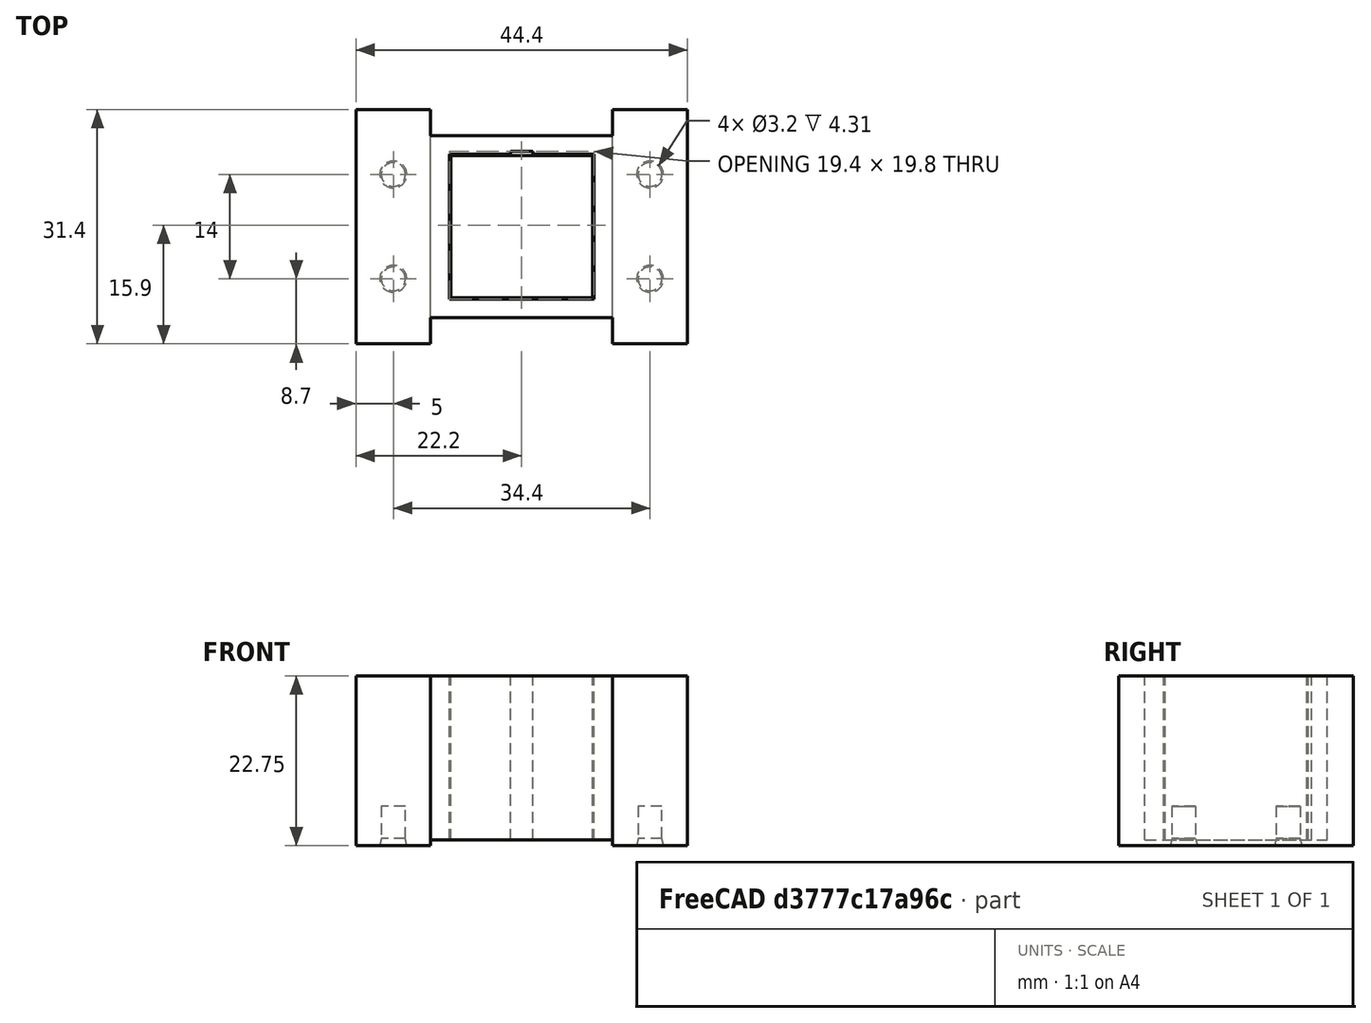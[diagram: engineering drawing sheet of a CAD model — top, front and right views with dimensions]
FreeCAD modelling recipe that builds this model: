
FCSTD DOCUMENT  (FreeCAD 1.0R39319 (Git))
Label: Main
License: All rights reserved
LicenseURL: https://en.wikipedia.org/wiki/All_rights_reserved
objects: Part::Fuse×20, Part::Box×12, Part::Cylinder×8, Part::Cone×4, Mesh::Feature×4, Part::Feature×4, Part::Cut×3, Part::MultiFuse×1
note: 52 computed .brp shape members not serialized (recipe doc carries the construction recipe); baked Part::Feature solids carry a one-line shape summary decoded from their .brp

FEATURE [Part::Box] cube
  AttacherType = Attacher::AttachEngine3D
  Height = 22
  Length = 24.4
  Placement = pos=(-12.2,-12.2,-11) rot=(0,0,1;0rad)
  Width = 24.4
FEATURE [Part::Box] cube001
  AttacherType = Attacher::AttachEngine3D
  Height = 23
  Length = 19.4
  Placement = pos=(-9.7,-9.7,-11.5) rot=(0,0,1;0rad)
  Width = 19.4
FEATURE [Part::Box] cube002
  AttacherType = Attacher::AttachEngine3D
  Height = 23
  Length = 3
  Placement = pos=(-1.5,9.7,-11.5) rot=(0,0,1;0rad)
  Width = 0.4
FEATURE [Part::Fuse] union
  Base = -> cube001
  Refine = true
  Tool = -> cube002
FEATURE [Part::Cut] difference
  Base = -> cube
  Placement = pos=(0,0,11.75) rot=(0,0,1;0rad)
  Refine = true
  Tool = -> union
FEATURE [Part::Box] cube003
  AttacherType = Attacher::AttachEngine3D
  Height = 22.75
  Length = 10
  Placement = pos=(-22.2,-15.7,0) rot=(0,0,1;0rad)
  Width = 31.4
FEATURE [Part::Cylinder] cylinder
  Angle = 360
  AttacherType = Attacher::AttachEngine3D
  FirstAngle = 0
  Height = 6
  Placement = pos=(-17.2,-7,0) rot=(0,0,1;0rad)
  Radius = 3.6
  SecondAngle = 0
FEATURE [Part::Cylinder] cylinder001
  Angle = 360
  AttacherType = Attacher::AttachEngine3D
  FirstAngle = 0
  Height = 6
  Placement = pos=(-17.2,7,0) rot=(0,0,1;0rad)
  Radius = 3.6
  SecondAngle = 0
FEATURE [Part::Fuse] Group
  Base = -> cylinder
  Refine = true
  Tool = -> cylinder001
FEATURE [Part::Fuse] union001
  Base = -> cube003
  Refine = true
  Tool = -> Group
FEATURE [Part::Cylinder] cylinder002
  Angle = 360
  AttacherType = Attacher::AttachEngine3D
  FirstAngle = 0
  Height = 5.32
  Placement = pos=(0,0,-0.01) rot=(0,0,1;0rad)
  Radius = 1.6
  SecondAngle = 0
FEATURE [Part::Cone] cylinder003
  Angle = 360
  AttacherType = Attacher::AttachEngine3D
  Height = 1
  Radius1 = 1.8
  Radius2 = 1.6
FEATURE [Part::Fuse] union002
  Base = -> cylinder002
  Placement = pos=(-17.2,-7,0) rot=(0,0,1;0rad)
  Refine = true
  Tool = -> cylinder003
FEATURE [Part::Cylinder] cylinder004
  Angle = 360
  AttacherType = Attacher::AttachEngine3D
  FirstAngle = 0
  Height = 5.32
  Placement = pos=(0,0,-0.01) rot=(0,0,1;0rad)
  Radius = 1.6
  SecondAngle = 0
FEATURE [Part::Cone] cylinder005
  Angle = 360
  AttacherType = Attacher::AttachEngine3D
  Height = 1
  Radius1 = 1.8
  Radius2 = 1.6
FEATURE [Part::Fuse] union003
  Base = -> cylinder004
  Placement = pos=(-17.2,7,0) rot=(0,0,1;0rad)
  Refine = true
  Tool = -> cylinder005
FEATURE [Part::Fuse] Group001
  Base = -> union002
  Refine = true
  Tool = -> union003
FEATURE [Part::Cut] difference001
  Base = -> union001
  Refine = true
  Tool = -> Group001
FEATURE [Part::Box] cube004
  AttacherType = Attacher::AttachEngine3D
  Height = 22.75
  Length = 10
  Placement = pos=(12.2,-15.7,0) rot=(0,0,1;0rad)
  Width = 31.4
FEATURE [Part::Cylinder] cylinder006
  Angle = 360
  AttacherType = Attacher::AttachEngine3D
  FirstAngle = 0
  Height = 6
  Placement = pos=(17.2,-7,0) rot=(0,0,1;0rad)
  Radius = 3.6
  SecondAngle = 0
FEATURE [Part::Cylinder] cylinder007
  Angle = 360
  AttacherType = Attacher::AttachEngine3D
  FirstAngle = 0
  Height = 6
  Placement = pos=(17.2,7,0) rot=(0,0,1;0rad)
  Radius = 3.6
  SecondAngle = 0
FEATURE [Part::Fuse] Group002
  Base = -> cylinder006
  Refine = true
  Tool = -> cylinder007
FEATURE [Part::Fuse] union004
  Base = -> cube004
  Refine = true
  Tool = -> Group002
FEATURE [Part::Cylinder] cylinder008
  Angle = 360
  AttacherType = Attacher::AttachEngine3D
  FirstAngle = 0
  Height = 5.32
  Placement = pos=(0,0,-0.01) rot=(0,0,1;0rad)
  Radius = 1.6
  SecondAngle = 0
FEATURE [Part::Cone] cylinder009
  Angle = 360
  AttacherType = Attacher::AttachEngine3D
  Height = 1
  Radius1 = 1.8
  Radius2 = 1.6
FEATURE [Part::Fuse] union005
  Base = -> cylinder008
  Placement = pos=(17.2,-7,0) rot=(0,0,1;0rad)
  Refine = true
  Tool = -> cylinder009
FEATURE [Part::Cylinder] cylinder010
  Angle = 360
  AttacherType = Attacher::AttachEngine3D
  FirstAngle = 0
  Height = 5.32
  Placement = pos=(0,0,-0.01) rot=(0,0,1;0rad)
  Radius = 1.6
  SecondAngle = 0
FEATURE [Part::Cone] cylinder011
  Angle = 360
  AttacherType = Attacher::AttachEngine3D
  Height = 1
  Radius1 = 1.8
  Radius2 = 1.6
FEATURE [Part::Fuse] union006
  Base = -> cylinder010
  Placement = pos=(17.2,7,0) rot=(0,0,1;0rad)
  Refine = true
  Tool = -> cylinder011
FEATURE [Part::Fuse] Group003
  Base = -> union005
  Refine = true
  Tool = -> union006
FEATURE [Part::Cut] difference002
  Base = -> union004
  Refine = true
  Tool = -> Group003
FEATURE [Part::Fuse] Group004
  Base = -> difference001
  Refine = true
  Tool = -> difference002
FEATURE [Part::Fuse] union007
  Base = -> difference
  Refine = true
  Tool = -> Group004
FEATURE [Part::Box] cube005
  AttacherType = Attacher::AttachEngine3D
  Height = 22
  Length = 19
  Placement = pos=(-9.5,-9.5,-11) rot=(0,0,1;0rad)
  Width = 19
FEATURE [Part::Box] cube006
  AttacherType = Attacher::AttachEngine3D
  Height = 22
  Length = 8
  Placement = pos=(-8.5,-8.5,-11) rot=(0,0,1;0rad)
  Width = 8
FEATURE [Part::Box] cube007
  AttacherType = Attacher::AttachEngine3D
  Height = 22
  Length = 8
  Placement = pos=(-8.5,0.5,-11) rot=(0,0,1;0rad)
  Width = 8
FEATURE [Part::Fuse] Group005
  Base = -> cube006
  Refine = true
  Tool = -> cube007
FEATURE [Part::Box] cube008
  AttacherType = Attacher::AttachEngine3D
  Height = 22
  Length = 8
  Placement = pos=(0.5,-8.5,-11) rot=(0,0,1;0rad)
  Width = 8
FEATURE [Part::Box] cube009
  AttacherType = Attacher::AttachEngine3D
  Height = 22
  Length = 8
  Placement = pos=(0.5,0.5,-11) rot=(0,0,1;0rad)
  Width = 8
FEATURE [Part::Fuse] Group006
  Base = -> cube008
  Refine = true
  Tool = -> cube009
FEATURE [Part::Fuse] Group007
  Base = -> Group005
  Refine = true
  Tool = -> Group006
FEATURE [Part::Box] cube010
  AttacherType = Attacher::AttachEngine3D
  Height = 22
  Length = 1
  Placement = pos=(-0.5,-9,-11) rot=(0,0,1;0rad)
  Width = 18
FEATURE [Part::Box] cube011
  AttacherType = Attacher::AttachEngine3D
  Height = 22
  Length = 18
  Placement = pos=(-9,-0.5,-11) rot=(0,0,1;0rad)
  Width = 1
FEATURE [Part::Fuse] Group008
  Base = -> cube010
  Refine = true
  Tool = -> cube011
FEATURE [Part::MultiFuse] Group009
  Placement = pos=(0,0,11.75) rot=(0,0,1;0rad)
  Refine = true
  Shapes = -> [cube005,Group007,Group008]
FEATURE [Mesh::Feature] MICROFC_60035_SMT_TR1  label="MICROFC-60035-SMT-TR1"
FEATURE [Part::Feature] FailedMeshImport
  Placement = pos=(-3.6,-3.6,0) rot=(1,0,0;1.5708rad)
FEATURE [Mesh::Feature] MICROFC_60035_SMT_TR002  label="MICROFC-60035-SMT-TR002"
FEATURE [Part::Feature] FailedMeshImport001
  Placement = pos=(-3.6,3.6,0) rot=(1,0,0;1.5708rad)
FEATURE [Part::Fuse] Group010
  Base = -> FailedMeshImport
  Refine = true
  Tool = -> FailedMeshImport001
FEATURE [Mesh::Feature] MICROFC_60035_SMT_TR003  label="MICROFC-60035-SMT-TR003"
FEATURE [Part::Feature] FailedMeshImport002
  Placement = pos=(3.6,-3.6,0) rot=(1,0,0;1.5708rad)
FEATURE [Mesh::Feature] MICROFC_60035_SMT_TR004  label="MICROFC-60035-SMT-TR004"
FEATURE [Part::Feature] FailedMeshImport003
  Placement = pos=(3.6,3.6,0) rot=(1,0,0;1.5708rad)
FEATURE [Part::Fuse] Group011
  Base = -> FailedMeshImport002
  Refine = true
  Tool = -> FailedMeshImport003
FEATURE [Part::Fuse] Group012
  Base = -> Group010
  Refine = true
  Tool = -> Group011
